# Revit family: agtatec_Record_SldngDrset_D-TSA-Telescopic_Standalone
name_source: partatom
category: Doors
revit_build: Autodesk Revit Architecture 2015 (Build: 20140606_1530(x64)
units: mm (PartAtom-declared; Revit-internal decimal feet)

## types (12) — shared parameters
AccessoryOptions = Contact manufacturer
AcousticRating = None
AlternativeDoorsetGlazing = Part of glazing spec
AntiFingerTrapRequirement = Yes
Assembly Code = B2030110
BIMObjectName = agtatec_Record_SlidingDoorset_D-TSA-Telescopic_Standalone
CenterOfDoor = 1000 mm  [stored 3.28084 ft]
CladdingProfile = Yes
ClearHeightOfPassage = 2187 mm  [stored 7.1752 ft]
ClearanceZones = No
Colour = Customer specific
Configuration = 1 or 2
Construction Type = Automatic Sliding Door
Description = Automatic Sliding Door
DistanceToWall = 57 mm  [stored 0.187008 ft]
DoorIncluded = Yes
DoorOpening2 = 600 mm
DoorSeal = yes
DoorsetFasteners = Screws
DoorsetOperation = Automatic
DriveDepth = 259 mm  [stored 0.849738 ft]
DriveDepth2 = 37 mm  [stored 0.121391 ft]
DriveUnit = agtatec_Record_Sliding Door, Sheet Metal (Painted Steel)
DriveUnitCenterDistance = 1000 mm  [stored 3.28084 ft]
ElectronicLock = Yes
Finish = Powder coated, Anodized, customer specific
FireExit = No
FireRating = None
FloorGuide = agtatec_Record_Sliding Door, Stainless Steel
FrameMaterial = Aluminium
FrameProfile = Aluminium
FrameSeal = Yes
Function = Exterior
GlassLayers = 2
GlassThickness1 = 6 mm (default)
GlassThickness2 = 6 mm (default)
GlassType = Part of glazing spec
GlazingAreaFraction = Depends on size. Can be calculated
HandicapAccessible = Yes
HasDrive = Yes
IfcExportAs = IfcDoorStyle
IfcExportType = Door
InnerPanelWidth1 = 332 mm
InnerPanelWidth2 = 320 mm  [stored 1.04987 ft]
InterlancingProfileHeight = 2195 mm  [stored 7.20144 ft]
IsExternal = Yes
LeafColourOptions = All RAL, customer specific
ManufacturerName = Record
ManufacturerURL = www.agta-record.com
Material = Aluminium
Model = record Telescopic Linear Slider
ModelReference = Depends on the configuration
NBSDescription = Sliding Doorset
NBSReference = 25-50-20/175
Name = SldngDrset_D-TSA-Telescopic_Standalone_Record
OpeningWidth = 1200 mm
OuterPanelWidthLeft = 373 mm  [stored 1.22375 ft]
OuterPanelWidthRight = 373 mm  [stored 1.22375 ft]
PanelFill = agtatec_Record_Sliding Door, Laminated Safety Glass (Clear)
PanelFrames = agtatec_Record_Sliding Door, Aluminium
PanelHeight = 2200 mm
Passage Mounting Left = No
Passage Mounting Right = No
PassageMountingProfile(OnlyApplicableForTypesWithTwoSidePanels) = No
ProductInformation = www.agta-record.com
ReferenceStandard = EN16005, EN16361, DIN 18650, etc.
ReplacementCost = Depends on the configuration and door type
SecurityRating = None
SelfClosing = Yes
ServiceLifeDuration = 10-15 years
Shape = Rectangular
SidePanelWidthLeft = 400 mm  [stored 1.31234 ft]
SidePanelWidthRight = 400 mm  [stored 1.31234 ft]
SmokeStop = No
SupportLength = 2000 mm  [stored 6.56168 ft]
ThresholdRequired = Yes
ThresholdStripping = No additional required, part of the doorset
URL = www.agta-record.com
Uniclass2 = Ss_25_30_20_77
Version = Version 1.0
WallMountingProfile = Yes
WarrantyDescription = Depends on country
WarrantyDurationLabour = Depends on country
WarrantyDurationParts = Depends on country
WarrantyDurationUnit = Depends on country
WarrantyGuarantorLabour = Local door manufacturer
WarrantyGuarantorParts = Local door manufacturer
Weight = Depends on configuration and size
WithDriveCladding = Yes
WithinStandardSizes = Yes
WithoutDriveCladding(OnlyApplicableForTypesWithoutSidePanels) = No
zero-valued in all types: Cost, DoorOpening, DoorOpening1, DriveUnitExtraWidthLeft, DriveUnitExtraWidthRight, ExtraLeft, ExtraRight, ExtraWidthLeft, ExtraWidthRight, NominalLength, ThermalTransmittance, Thickness

## per-type parameters (varying)
| type | CladdingVoid | ClearanceZoneLeft | ClearanceZoneRight | DriveUnitHeight | DurationUnit | Height | LeftPanel | NominalHeight | NominalWidth | RightPanel | Rough Height | Rough Width | TotalHeight | TotalWidth | Wall Mounting Left | Wall Mounting Right | Width | With side panels | Without side panels |
| D-TSA 150 mm drive unit height - with two side panels | 35 mm  [stored 0.114829 ft] | 1016 mm | 1016 mm | 150 mm  [stored 0.492126 ft] | year | 2337 mm  [stored 7.66732 ft] | Yes | 2337 mm  [stored 7.66732 ft] | 2000 mm  [stored 6.56168 ft] | Yes | 2343 mm  [stored 7.68701 ft] | 2006 mm  [stored 6.58136 ft] | 2337 mm  [stored 7.66732 ft] | 2000 mm  [stored 6.56168 ft] | Yes | Yes | 2000 mm  [stored 6.56168 ft] | Yes | No |
| D-TSA 108 mm drive unit height - side panel left | 35 mm  [stored 0.114829 ft] | 1016 mm | 1000 mm  [stored 3.28084 ft] | 108 mm  [stored 0.354331 ft] | year | 2295 mm | Yes | 2295 mm | 1644 mm  [stored 5.3937 ft] | No | 2301 mm | 1650 mm  [stored 5.41339 ft] | 2295 mm | 1644 mm  [stored 5.3937 ft] | Yes | No | 1644 mm  [stored 5.3937 ft] | No | No |
| D-TSA 108 mm drive unit height - side panel right | 35 mm  [stored 0.114829 ft] | 1000 mm  [stored 3.28084 ft] | 1016 mm | 108 mm  [stored 0.354331 ft] | year | 2295 mm | No | 2295 mm | 1644 mm  [stored 5.3937 ft] | Yes | 2301 mm | 1650 mm  [stored 5.41339 ft] | 2295 mm | 1644 mm  [stored 5.3937 ft] | No | Yes | 1644 mm  [stored 5.3937 ft] | No | No |
| D-TSA 108 mm drive unit height - with two side panels | 35 mm  [stored 0.114829 ft] | 1016 mm | 1016 mm | 108 mm  [stored 0.354331 ft] | year | 2295 mm | Yes | 2295 mm | 2000 mm  [stored 6.56168 ft] | Yes | 2301 mm | 2006 mm  [stored 6.58136 ft] | 2295 mm | 2000 mm  [stored 6.56168 ft] | Yes | Yes | 2000 mm  [stored 6.56168 ft] | Yes | No |
| D-TSA 150 mm drive unit height - side panel left | 35 mm  [stored 0.114829 ft] | 1016 mm | 1000 mm  [stored 3.28084 ft] | 150 mm  [stored 0.492126 ft] | year | 2337 mm  [stored 7.66732 ft] | Yes | 2337 mm  [stored 7.66732 ft] | 1644 mm  [stored 5.3937 ft] | No | 2343 mm  [stored 7.68701 ft] | 1650 mm  [stored 5.41339 ft] | 2337 mm  [stored 7.66732 ft] | 1644 mm  [stored 5.3937 ft] | Yes | No | 1644 mm  [stored 5.3937 ft] | No | No |
| D-TSA 150 mm drive unit height - side panel right | 35 mm  [stored 0.114829 ft] | 1000 mm  [stored 3.28084 ft] | 1016 mm | 150 mm  [stored 0.492126 ft] | year | 2337 mm  [stored 7.66732 ft] | No | 2337 mm  [stored 7.66732 ft] | 1644 mm  [stored 5.3937 ft] | Yes | 2343 mm  [stored 7.68701 ft] | 1650 mm  [stored 5.41339 ft] | 2337 mm  [stored 7.66732 ft] | 1644 mm  [stored 5.3937 ft] | No | Yes | 1644 mm  [stored 5.3937 ft] | No | No |
| D-TSA 108 mm drive unit height - without side panels | 3 mm  [stored 0.00984252 ft] | 1000 mm  [stored 3.28084 ft] | 1000 mm  [stored 3.28084 ft] | 108 mm  [stored 0.354331 ft] | year | 2295 mm | No | 2295 mm | 1288 mm  [stored 4.22572 ft] | No | 2301 mm | 1294 mm  [stored 4.24541 ft] | 2295 mm | 1288 mm  [stored 4.22572 ft] | No | No | 1288 mm  [stored 4.22572 ft] | No | Yes |
| D-TSA 150 mm drive unit height - without side panels | 3 mm  [stored 0.00984252 ft] | 1000 mm  [stored 3.28084 ft] | 1000 mm  [stored 3.28084 ft] | 150 mm  [stored 0.492126 ft] | 1900-12-31T23:59:59 | 2337 mm  [stored 7.66732 ft] | No | 2337 mm  [stored 7.66732 ft] | 1288 mm  [stored 4.22572 ft] | No | 2343 mm  [stored 7.68701 ft] | 1294 mm  [stored 4.24541 ft] | 2337 mm  [stored 7.66732 ft] | 1288 mm  [stored 4.22572 ft] | No | No | 1288 mm  [stored 4.22572 ft] | No | Yes |
| D-TSA 200 mm drive unit height - side panel left | 35 mm  [stored 0.114829 ft] | 1016 mm | 1000 mm  [stored 3.28084 ft] | 200 mm  [stored 0.656168 ft] | 1900-12-31T23:59:59 | 2387 mm  [stored 7.83136 ft] | Yes | 2387 mm  [stored 7.83136 ft] | 1644 mm  [stored 5.3937 ft] | No | 2393 mm  [stored 7.85105 ft] | 1650 mm  [stored 5.41339 ft] | 2387 mm  [stored 7.83136 ft] | 1644 mm  [stored 5.3937 ft] | Yes | No | 1644 mm  [stored 5.3937 ft] | No | No |
| D-TSA 200 mm drive unit height - side panel right | 35 mm  [stored 0.114829 ft] | 1000 mm  [stored 3.28084 ft] | 1016 mm | 200 mm  [stored 0.656168 ft] | 1900-12-31T23:59:59 | 2387 mm  [stored 7.83136 ft] | No | 2387 mm  [stored 7.83136 ft] | 1644 mm  [stored 5.3937 ft] | Yes | 2393 mm  [stored 7.85105 ft] | 1650 mm  [stored 5.41339 ft] | 2387 mm  [stored 7.83136 ft] | 1644 mm  [stored 5.3937 ft] | No | Yes | 1644 mm  [stored 5.3937 ft] | No | No |
| D-TSA 200 mm drive unit height - with two side panels | 35 mm  [stored 0.114829 ft] | 1016 mm | 1016 mm | 200 mm  [stored 0.656168 ft] | year | 2387 mm  [stored 7.83136 ft] | Yes | 2387 mm  [stored 7.83136 ft] | 2000 mm  [stored 6.56168 ft] | Yes | 2393 mm  [stored 7.85105 ft] | 2006 mm  [stored 6.58136 ft] | 2387 mm  [stored 7.83136 ft] | 2000 mm  [stored 6.56168 ft] | Yes | Yes | 2000 mm  [stored 6.56168 ft] | Yes | No |
| D-TSA 200 mm drive unit height - without side panels | 3 mm  [stored 0.00984252 ft] | 1000 mm  [stored 3.28084 ft] | 1000 mm  [stored 3.28084 ft] | 200 mm  [stored 0.656168 ft] | year | 2387 mm  [stored 7.83136 ft] | No | 2387 mm  [stored 7.83136 ft] | 1288 mm  [stored 4.22572 ft] | No | 2393 mm  [stored 7.85105 ft] | 1294 mm  [stored 4.24541 ft] | 2387 mm  [stored 7.83136 ft] | 1288 mm  [stored 4.22572 ft] | No | No | 1288 mm  [stored 4.22572 ft] | No | Yes |

note: [stored X ft] marks values corroborated as IEEE doubles in the binary element streams (Revit-internal decimal feet)

## geometry (parser evidence)
native form markers: Sweep x15
no freeform markers — native parametric forms only
